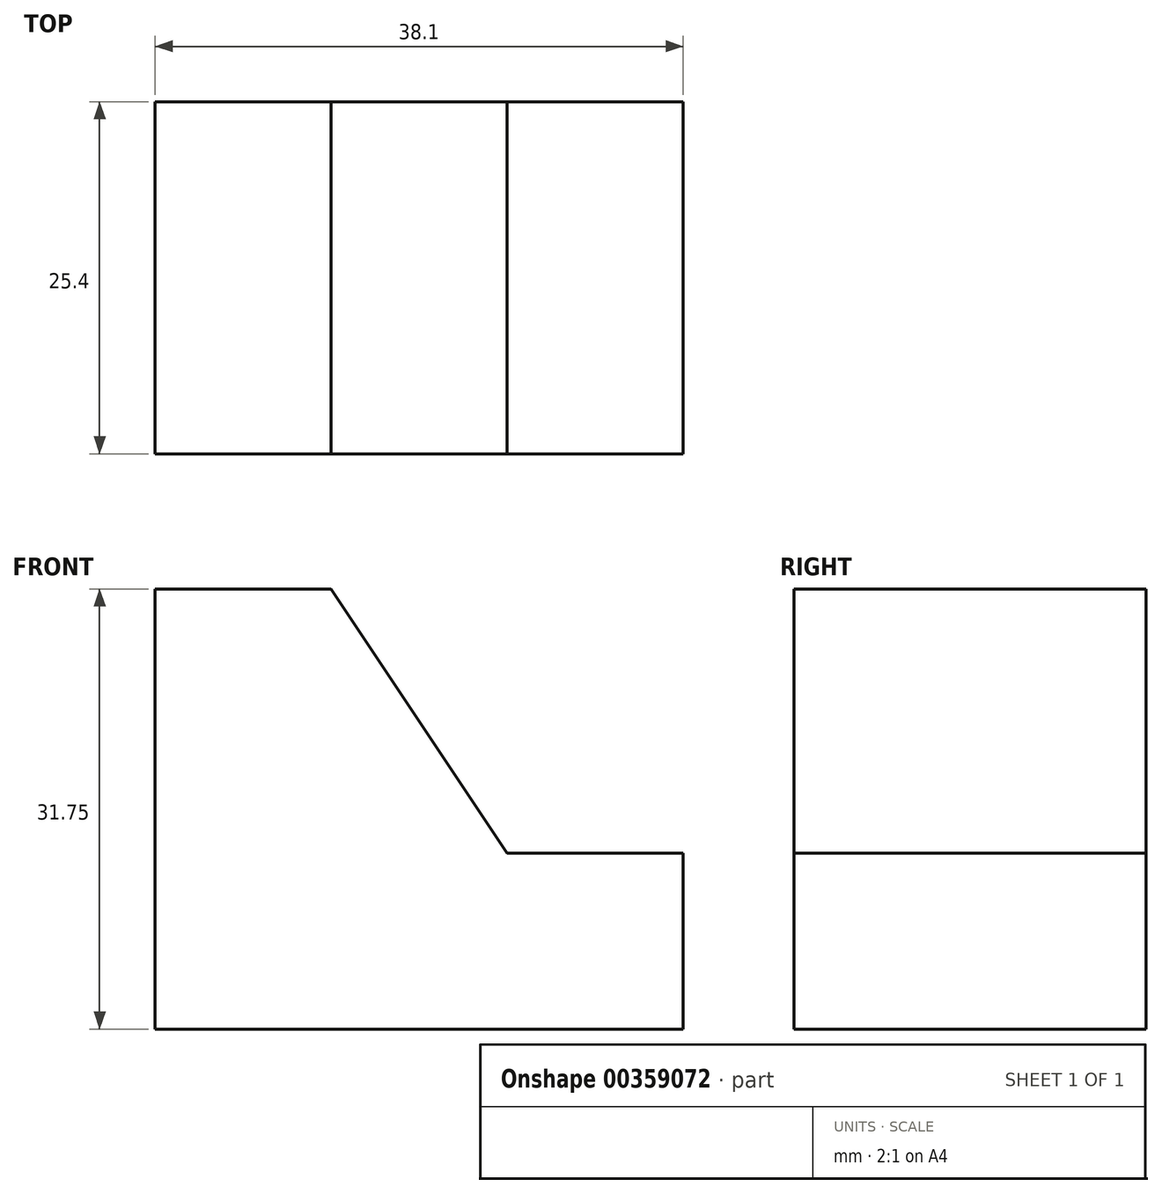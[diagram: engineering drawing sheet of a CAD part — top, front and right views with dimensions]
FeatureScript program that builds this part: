
annotation { "Feature Type Name" : "Feature", "Feature Type Description" : "" }
export const myFeature = defineFeature(function(context is Context, id is Id, definition is map)
    precondition{}
    {
        {
            var Q0;
            Q0=qCreatedBy(makeId("Front.planeOp"),FACE);
            var sketch = newSketch(context, id + "F0", { "sketchPlane" : qUnion([Q0])});
            skLineSegment(sketch, "E0", {"start": v(0, 31.75) * mm, "end": v(12.7, 31.75) * mm});
            skLineSegment(sketch, "E1", {"start": v(12.7, 31.75) * mm, "end": v(25.4, 12.7) * mm});
            skLineSegment(sketch, "E2", {"start": v(25.4, 12.7) * mm, "end": v(38.1, 12.7) * mm});
            skLineSegment(sketch, "E3", {"start": v(38.1, 12.7) * mm, "end": v(38.1, 0) * mm});
            skLineSegment(sketch, "E4", {"start": v(38.1, 0) * mm, "end": v(0, 0) * mm});
            skLineSegment(sketch, "E5", {"start": v(0, 0) * mm, "end": v(0, 31.75) * mm});
            skSolve(sketch);
        }
        {
            var Q0;
            Q0 = qSketchRegion(id + "F0", true);
            extrude(context, id + "F1", {"entities" : qUnion([Q0]), "depth" : 25.4 * mm});
        }
    });
